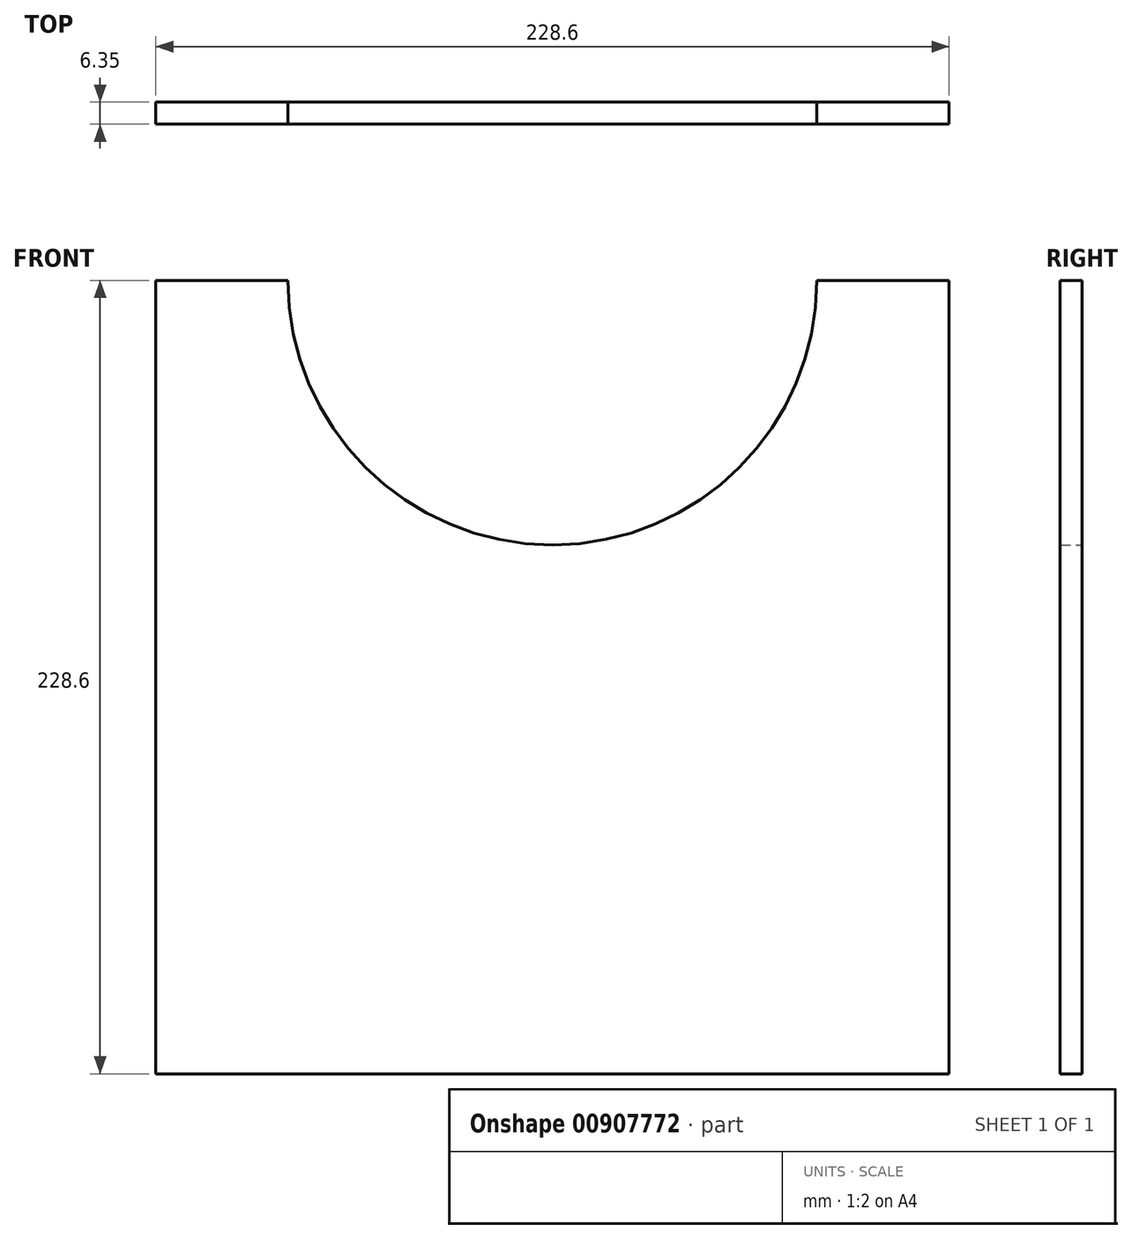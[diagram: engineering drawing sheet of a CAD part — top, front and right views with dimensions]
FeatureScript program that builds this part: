
annotation { "Feature Type Name" : "Feature", "Feature Type Description" : "" }
export const myFeature = defineFeature(function(context is Context, id is Id, definition is map)
    precondition{}
    {
        {
            var Q0;
            Q0=qCreatedBy(makeId("Front.planeOp"),FACE);
            var sketch = newSketch(context, id + "F0", { "sketchPlane" : qUnion([Q0])});
            skLineSegment(sketch, "E0.bottom", {"start": v(114.3, -114.3) * mm, "end": v(-114.3, -114.3) * mm});
            skLineSegment(sketch, "E0.top", {"start": v(114.3, 114.3) * mm, "end": v(76.2, 114.3) * mm});
            skLineSegment(sketch, "E0.left", {"start": v(114.3, -114.3) * mm, "end": v(114.3, 114.3) * mm});
            skLineSegment(sketch, "E0.right", {"start": v(-114.3, -114.3) * mm, "end": v(-114.3, 114.3) * mm});
            skPoint(sketch, "E0.middle", {"position": v(0, 0) * mm});
            skArc(sketch, "E1", {"start": v(-76.2, 114.3) * mm, "mid": v(0, 38.1) * mm, "end": v(76.2, 114.3) * mm});
            skLineSegment(sketch, "E2.trimOffspring", {"start": v(-76.2, 114.3) * mm, "end": v(-114.3, 114.3) * mm});
            skSolve(sketch);
        }
        {
            var Q0;
            Q0=makeQuery(id+"F0.imprint","IMPRINT",FACE,{"disambiguationData":[TD([[makeQuery(id+"F0.imprint","IMPRINT",EDGE,{"derivedFrom":sQuery(id+"F0.wireOp",EDGE,"E0.bottom")}),-1.0]])]});
            extrude(context, id + "F1", {"entities" : qUnion([Q0]), "depth" : 6.35 * mm, "offsetDistance" : 25.4 * mm});
        }
    });
